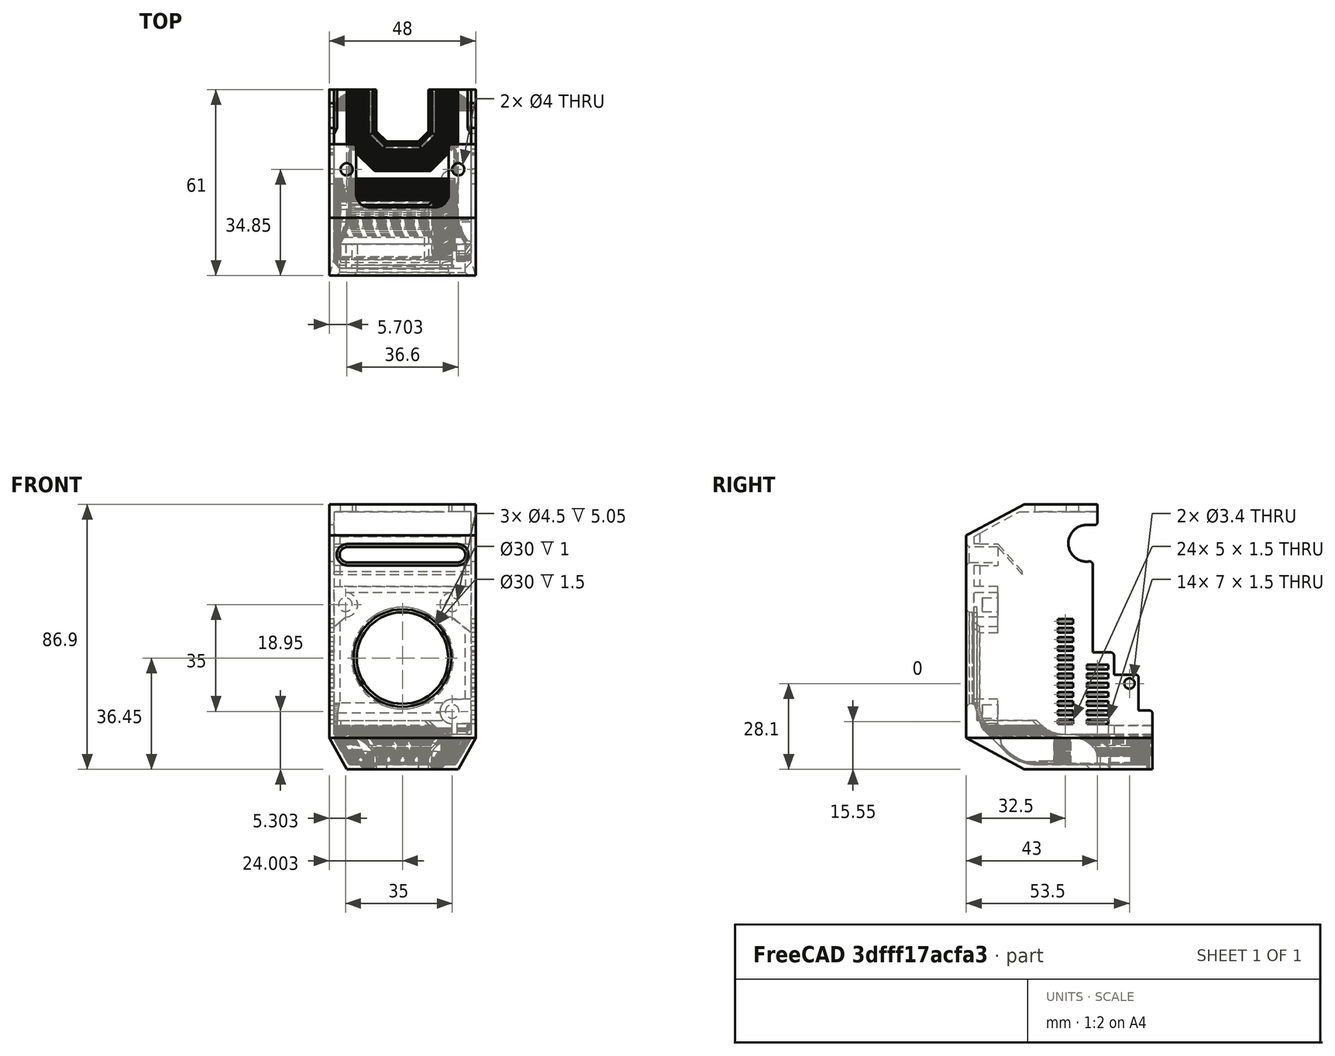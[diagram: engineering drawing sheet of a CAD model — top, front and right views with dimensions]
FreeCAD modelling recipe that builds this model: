
FCSTD DOCUMENT  (FreeCAD 1.0R38641 +468 (Git))
Label: k1_toolhead_cover
License: All rights reserved
LicenseURL: https://en.wikipedia.org/wiki/All_rights_reserved
objects: Part::Feature×1, PartDesign::FeatureBase×1, PartDesign::Body×1, App::Link×1, App::Part×1
note: 4 computed .brp shape members not serialized (recipe doc carries the construction recipe); baked Part::Feature solids carry a one-line shape summary decoded from their .brp
EXTERNAL_REF file=cad_4020.FCStd obj=Blower_Fan_4020_v019

FEATURE [Part::Feature] Part__Feature  label="step"
  shape: bbox 48 x 61 x 86.9 mm, 4783 faces (baked)
FEATURE [PartDesign::FeatureBase] BaseFeature
  BaseFeature = -> Part__Feature
  Suppressed = false
FEATURE [PartDesign::Body] Body  label="k1_toolhead_cover"
  AllowCompound = false
  BaseFeature = -> Part__Feature
  Group = -> [BaseFeature]
  Origin = -> Origin
  Tip = -> BaseFeature
FEATURE [App::Link] Link  label="cad_4020_link"
  LinkPlacement = pos=(371.302,112.64,-346.501) rot=(0,0,1;1.5708rad)
  LinkedObject = -> <external cad_4020.FCStd>#Blower_Fan_4020_v019
  Placement = pos=(371.302,112.64,-346.501) rot=(0,0,1;1.5708rad)
FEATURE [App::Part] Part  label="k1_toolhead_cover_part"
  Group = -> [Part__Feature,Body,Link]
  Origin = -> Origin001
